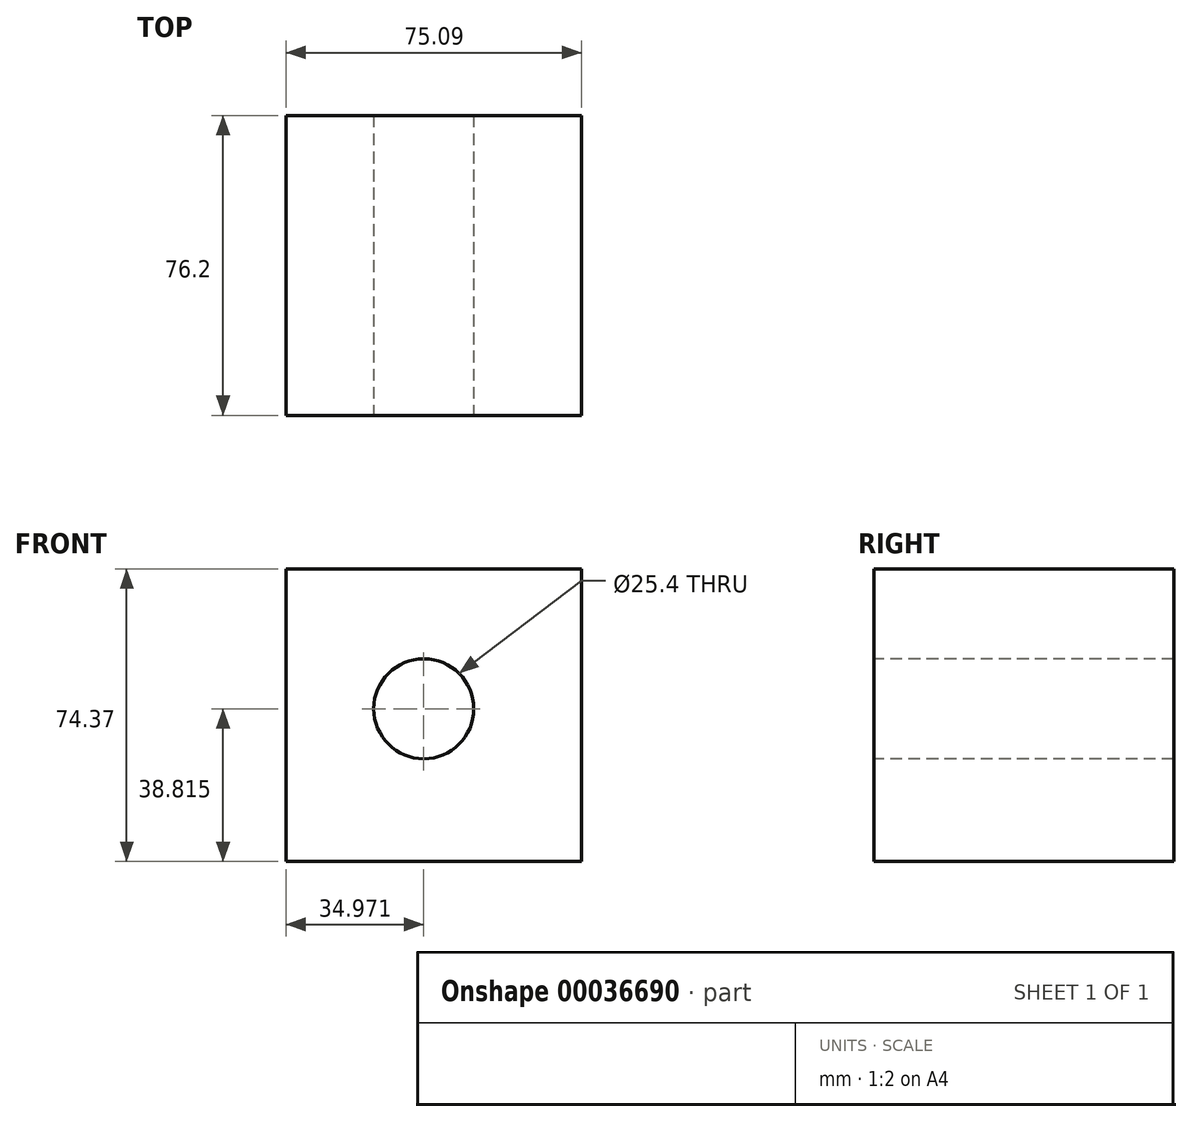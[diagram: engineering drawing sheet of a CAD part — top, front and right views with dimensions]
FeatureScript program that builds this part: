
annotation { "Feature Type Name" : "Feature", "Feature Type Description" : "" }
export const myFeature = defineFeature(function(context is Context, id is Id, definition is map)
    precondition{}
    {
        {
            var Q0;
            Q0=qCreatedBy(makeId("Front.planeOp"),FACE);
            var sketch = newSketch(context, id + "F0", { "sketchPlane" : qUnion([Q0])});
            skLineSegment(sketch, "E0.bottom", {"start": v(0, 0) * mm, "end": v(75.09, 0) * mm});
            skLineSegment(sketch, "E0.top", {"start": v(0, 74.37) * mm, "end": v(75.09, 74.37) * mm});
            skLineSegment(sketch, "E0.left", {"start": v(0, 0) * mm, "end": v(0, 74.37) * mm});
            skLineSegment(sketch, "E0.right", {"start": v(75.09, 0) * mm, "end": v(75.09, 74.37) * mm});
            skSolve(sketch);
        }
        {
            var Q0;
            Q0=makeQuery(id+"F0.imprint","IMPRINT",FACE,{"disambiguationData":[TD([[makeQuery(id+"F0.imprint","IMPRINT",EDGE,{"derivedFrom":sQuery(id+"F0.wireOp",EDGE,"E0.bottom")}),1.0]])]});
            extrude(context, id + "F1", {"entities" : qUnion([Q0]), "depth" : 76.2 * mm});
        }
        {
            var Q0;
            Q0=makeQuery(id+"F1.opExtrude","CAP_FACE",FACE,{"disambiguationData":[OSD([sQuery(id+"F0.wireOp",EDGE,"E0.bottom"),sQuery(id+"F0.wireOp",EDGE,"E0.top"),sQuery(id+"F0.wireOp",EDGE,"E0.left"),sQuery(id+"F0.wireOp",EDGE,"E0.right")])],"isStart":false});
            var sketch = newSketch(context, id + "F2", { "sketchPlane" : qUnion([Q0])});
            skPoint(sketch, "E1", {"position": v(34.97, 38.82) * mm});
            skSolve(sketch);
        }
        {
            var Q0;
            Q0=sQuery(id+"F2.wireOp",VERTEX,"E1");
            var Q1;
            Q1=makeQuery(id+"F1.opExtrude","SWEPT_BODY",BODY,{"disambiguationData":[OSD([sQuery(id+"F0.wireOp",EDGE,"E0.bottom"),sQuery(id+"F0.wireOp",EDGE,"E0.top"),sQuery(id+"F0.wireOp",EDGE,"E0.left"),sQuery(id+"F0.wireOp",EDGE,"E0.right")])]});
            hole(context, id + "F3", {"style" : HoleStyle.SIMPLE, "holeDiameter" : 25.4 * mm, "endStyle" : HoleEndStyle.THROUGH, "locations" : qUnion([Q0]), "scope" : qUnion([Q1])});
        }
    });
